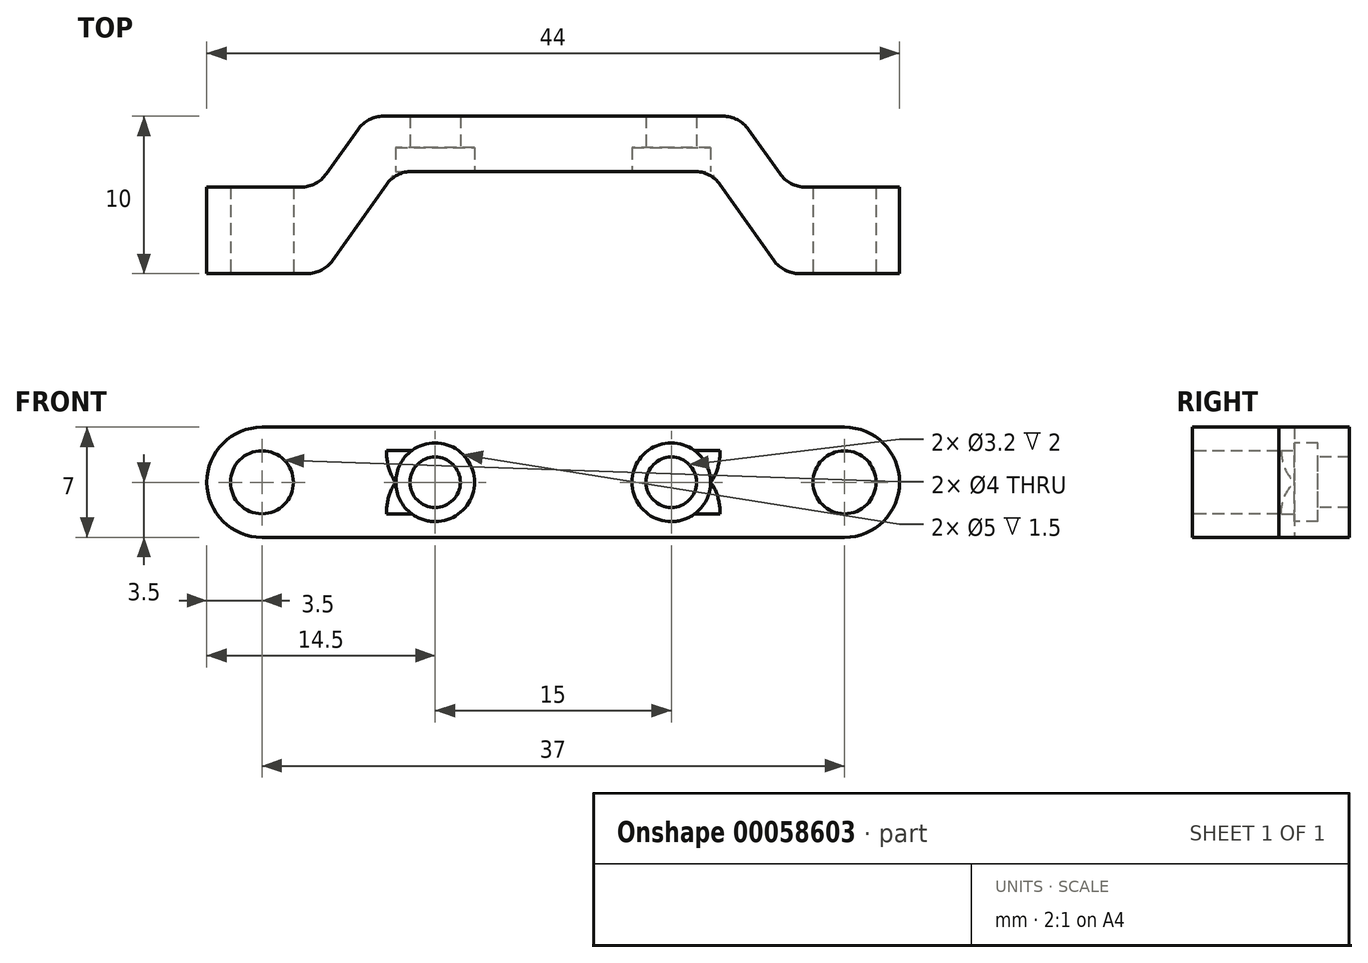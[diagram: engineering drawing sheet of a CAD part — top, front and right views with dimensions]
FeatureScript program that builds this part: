
annotation { "Feature Type Name" : "Feature", "Feature Type Description" : "" }
export const myFeature = defineFeature(function(context is Context, id is Id, definition is map)
    precondition{}
    {
        {
            var Q0;
            Q0=qCreatedBy(makeId("Top.planeOp"),FACE);
            var sketch = newSketch(context, id + "F0", { "sketchPlane" : qUnion([Q0])});
            skLineSegment(sketch, "E0", {"start": v(-22, 0) * mm, "end": v(-14.6, 0) * mm});
            skLineSegment(sketch, "E1", {"start": v(-14.6, 0) * mm, "end": v(-10, 6.5) * mm});
            skLineSegment(sketch, "E2", {"start": v(-10, 6.5) * mm, "end": v(0, 6.5) * mm});
            skLineSegment(sketch, "E3", {"start": v(0, 6.5) * mm, "end": v(0, 10) * mm});
            skLineSegment(sketch, "E4", {"start": v(0, 10) * mm, "end": v(-11.8, 10) * mm});
            skLineSegment(sketch, "E5", {"start": v(-11.8, 10) * mm, "end": v(-15, 5.5) * mm});
            skLineSegment(sketch, "E6", {"start": v(-15, 5.5) * mm, "end": v(-22, 5.5) * mm});
            skLineSegment(sketch, "E7", {"start": v(-22, 5.5) * mm, "end": v(-22, 0) * mm});
            skSolve(sketch);
        }
        {
            var Q0;
            Q0=makeQuery(id+"F0.imprint","IMPRINT",FACE,{"disambiguationData":[TD([[makeQuery(id+"F0.imprint","IMPRINT",EDGE,{"derivedFrom":sQuery(id+"F0.wireOp",EDGE,"E0")}),1.0]])]});
            extrude(context, id + "F1", {"entities" : qUnion([Q0]), "endBound" : BoundingType.SYMMETRIC, "depth" : 7 * mm});
        }
        {
            var Q0;
            Q0=makeQuery(id+"F1.opExtrude","CAP_EDGE",EDGE,{"disambiguationData":[OSD([sQuery(id+"F0.wireOp",EDGE,"E7")])],"isStart":false});
            var Q1;
            Q1=makeQuery(id+"F1.opExtrude","CAP_EDGE",EDGE,{"disambiguationData":[OSD([sQuery(id+"F0.wireOp",EDGE,"E7")])],"isStart":true});
            fillet(context, id + "F2", {"entities" : qUnion([Q0, Q1]), "radius" : 3.5 * mm, "tangentPropagation" : true, "allowEdgeOverflow" : false});
        }
        {
            var Q0;
            Q0=makeQuery(id+"F1.opExtrude","SWEPT_FACE",FACE,{"disambiguationData":[OSD([sQuery(id+"F0.wireOp",EDGE,"E0")])]});
            var sketch = newSketch(context, id + "F3", { "sketchPlane" : qUnion([Q0])});
            skCircle(sketch, "E8", {"center": v(-18.5, 0) * mm, "radius": 2 * mm});
            skCircle(sketch, "E9", {"center": v(-7.5, 0) * mm, "radius": 1.6 * mm});
            skSolve(sketch);
        }
        {
            var Q0;
            Q0=makeQuery(id+"F3.imprint","IMPRINT",FACE,{"disambiguationData":[TD([[makeQuery(id+"F3.imprint","IMPRINT",EDGE,{"derivedFrom":sQuery(id+"F3.wireOp",EDGE,"E8")}),1.0]])]});
            var Q1;
            Q1=makeQuery(id+"F3.imprint","IMPRINT",FACE,{"disambiguationData":[TD([[makeQuery(id+"F3.imprint","IMPRINT",EDGE,{"derivedFrom":sQuery(id+"F3.wireOp",EDGE,"E9")}),1.0]])]});
            extrude(context, id + "F4", {"entities" : qUnion([Q0, Q1]), "operationType" : NewBodyOperationType.REMOVE, "endBound" : BoundingType.THROUGH_ALL, "oppositeDirection" : true, "depth" : 25 * mm});
        }
        {
            var Q0;
            Q0=makeQuery(id+"F1.opExtrude","SWEPT_FACE",FACE,{"disambiguationData":[OSD([sQuery(id+"F0.wireOp",EDGE,"E2")])]});
            var sketch = newSketch(context, id + "F5", { "sketchPlane" : qUnion([Q0])});
            skCircle(sketch, "E10", {"center": v(-7.5, 0) * mm, "radius": 2.5 * mm});
            skSolve(sketch);
        }
        {
            var Q0;
            Q0=makeQuery(id+"F5.imprint","IMPRINT",FACE,{"disambiguationData":[TD([[makeQuery(id+"F5.imprint","IMPRINT",EDGE,{"derivedFrom":sQuery(id+"F5.wireOp",EDGE,"E10")}),1.0]])]});
            extrude(context, id + "F6", {"entities" : qUnion([Q0]), "operationType" : NewBodyOperationType.REMOVE, "oppositeDirection" : true, "depth" : 1.5 * mm});
        }
        {
            var Q0;
            Q0=makeQuery(id+"F1.opExtrude","SWEPT_EDGE",EDGE,{"disambiguationData":[OSD([sQuery(id+"F0.wireOp",EDGE,"E0"),sQuery(id+"F0.wireOp",EDGE,"E1")])]});
            var Q1;
            {var subQ0=sQuery(id+"F0.wireOp",EDGE,"E2");var subQ1=sQuery(id+"F0.wireOp",EDGE,"E1");Q1=makeQuery(id+"F6.boolean.opBoolean","SPLIT",EDGE,{"disambiguationData":[TD([makeQuery(id+"F1.opExtrude","CAP_FACE",FACE,{"disambiguationData":[OSD([sQuery(id+"F0.wireOp",EDGE,"E0"),subQ1,subQ0,sQuery(id+"F0.wireOp",EDGE,"E3"),sQuery(id+"F0.wireOp",EDGE,"E4"),sQuery(id+"F0.wireOp",EDGE,"E5"),sQuery(id+"F0.wireOp",EDGE,"E6"),sQuery(id+"F0.wireOp",EDGE,"E7")])],"isStart":false})])],"derivedFrom":makeQuery(id+"F1.opExtrude","SWEPT_EDGE",EDGE,{"disambiguationData":[OSD([subQ1,subQ0])]})});}
            var Q2;
            {var subQ0=sQuery(id+"F0.wireOp",EDGE,"E2");var subQ1=sQuery(id+"F0.wireOp",EDGE,"E1");Q2=makeQuery(id+"F6.boolean.opBoolean","SPLIT",EDGE,{"disambiguationData":[TD([makeQuery(id+"F1.opExtrude","CAP_FACE",FACE,{"disambiguationData":[OSD([sQuery(id+"F0.wireOp",EDGE,"E0"),subQ1,subQ0,sQuery(id+"F0.wireOp",EDGE,"E3"),sQuery(id+"F0.wireOp",EDGE,"E4"),sQuery(id+"F0.wireOp",EDGE,"E5"),sQuery(id+"F0.wireOp",EDGE,"E6"),sQuery(id+"F0.wireOp",EDGE,"E7")])],"isStart":true})])],"derivedFrom":makeQuery(id+"F1.opExtrude","SWEPT_EDGE",EDGE,{"disambiguationData":[OSD([subQ1,subQ0])]})});}
            var Q3;
            Q3=makeQuery(id+"F1.opExtrude","SWEPT_EDGE",EDGE,{"disambiguationData":[OSD([sQuery(id+"F0.wireOp",EDGE,"E5"),sQuery(id+"F0.wireOp",EDGE,"E6")])]});
            var Q4;
            Q4=makeQuery(id+"F1.opExtrude","SWEPT_EDGE",EDGE,{"disambiguationData":[OSD([sQuery(id+"F0.wireOp",EDGE,"E4"),sQuery(id+"F0.wireOp",EDGE,"E5")])]});
            fillet(context, id + "F7", {"entities" : qUnion([Q0, Q1, Q2, Q3, Q4]), "radius" : 2 * mm, "tangentPropagation" : true, "allowEdgeOverflow" : false});
        }
        {
            var Q0;
            Q0=makeQuery(id+"F1.opExtrude","SWEPT_BODY",BODY,{"disambiguationData":[OSD([sQuery(id+"F0.wireOp",EDGE,"E0"),sQuery(id+"F0.wireOp",EDGE,"E1"),sQuery(id+"F0.wireOp",EDGE,"E2"),sQuery(id+"F0.wireOp",EDGE,"E3"),sQuery(id+"F0.wireOp",EDGE,"E4"),sQuery(id+"F0.wireOp",EDGE,"E5"),sQuery(id+"F0.wireOp",EDGE,"E6"),sQuery(id+"F0.wireOp",EDGE,"E7")])]});
            var Q1;
            Q1=qCreatedBy(makeId("Right.planeOp"),FACE);
            mirror(context, id + "F8", {"operationType" : NewBodyOperationType.ADD, "entities" : qUnion([Q0]), "mirrorPlane" : qUnion([Q1])});
        }
    });
